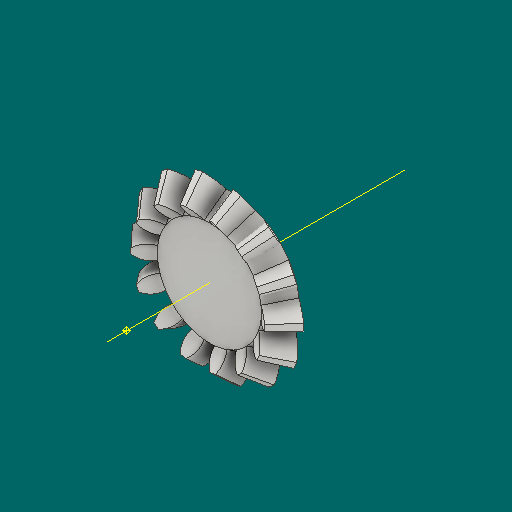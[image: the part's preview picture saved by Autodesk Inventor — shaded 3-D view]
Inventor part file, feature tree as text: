
AUTODESK INVENTOR PART (.ipt)
format: ipt  version: 2023.1 (Build 271208000, 208)  size: 458,240 bytes
history: native  units: mm
features: other x24, loft x2, pattern_circular x2, sketch x1
ambient origin geometry x6: Origin, XZ Plane, X Axis, Y Axis, Z Axis, Center Point
bodies: Solid1 (feature_tree)
feature tree (29):
  other  "Top Point"
  other  "Mesh Plane2"
  other  "Teeth Body"
  other  "Start Point"
  other  "Tooth Plane"
  other  "Start Sketch"
  other  "End Point"
  other  "3D Sketch Right"
  other  "End Plane Right"
  loft  "Loft Right"
  pattern_circular  "Circular Pattern Right"  [2 undecoded]
  other  "3D Sketch Left"
  other  "End Plane Left"
  loft  "Loft Left"
  pattern_circular  "Circular Pattern Left"  [2 undecoded]
  other  "Fix Body"
  other  "Mesh Plane"
  other  "Top Plane"
  other  "Teeth Body Sketch"
  other  "End Plane"
  other  "End Sketch"
  other  "Helical Curve Left"
  other  "End Sketch Left"
  other  "Body Sketch"
  sketch  "Sketch6"  dims[d0=17.78mm d1=15.374054mm d2=19.784955mm d3=3.175mm d4=10.650295mm d5=90.0deg d7=3.377532mm d8=4.137362mm d9=9.977079mm d11=3.3147mm d12=2.604374mm d15=3.19027mm d16=7.693204mm d17=0.0mm d18=90.0deg d19=0.0mm d20=90.0deg d21=140.0mm d22=360.0deg d26=111.138613mm d27=2.616466mm d28=17.78mm d29=-6.610432mm d30=2.604374mm d31=3.19027mm d32=7.693204mm d35=0.0mm d37=0.0mm d39=0.0mm d40=90.0deg d41=140.0mm d42=360.0deg d46=90.0deg d47=90.0deg d48=0.0mm d49=0.0mm d50=90.0deg d51=2.243995mm d52=0.0mm d53=0.0mm d54=0.0mm d56=6.097357mm d57=13.370599mm d58=9.403119mm d59=10.309907mm d60=7.250631mm d61=10.309907mm d62=7.250631mm d63=90.0deg d64=90.0deg d65=111.138613mm d66=31.5mm d67=17.78mm d68=-6.610432mm d69=2.616466mm d70=3.19027mm d71=7.693204mm d72=2.604374mm d73=7.250631mm d74=10.309907mm d75=0.0mm d76=90.0deg d77=0.0mm d78=90.0deg d79=0.0mm d80=90.0deg d81=140.0mm d82=360.0deg d84=10.0mm d85=20.0mm d86=20.0mm d87=10.0mm d88=0.0mm d89=0.0mm]
  other  "Srf1"
  other  "Helical Curve Right"
  other  "End Sketch Right"
  other  "Pitch Diameter"
note: 4 required parameter values undecoded (feature->parameter linkage not recoverable at this tier; creation-order binding heuristic only, values carry confidence <= 0.55)
